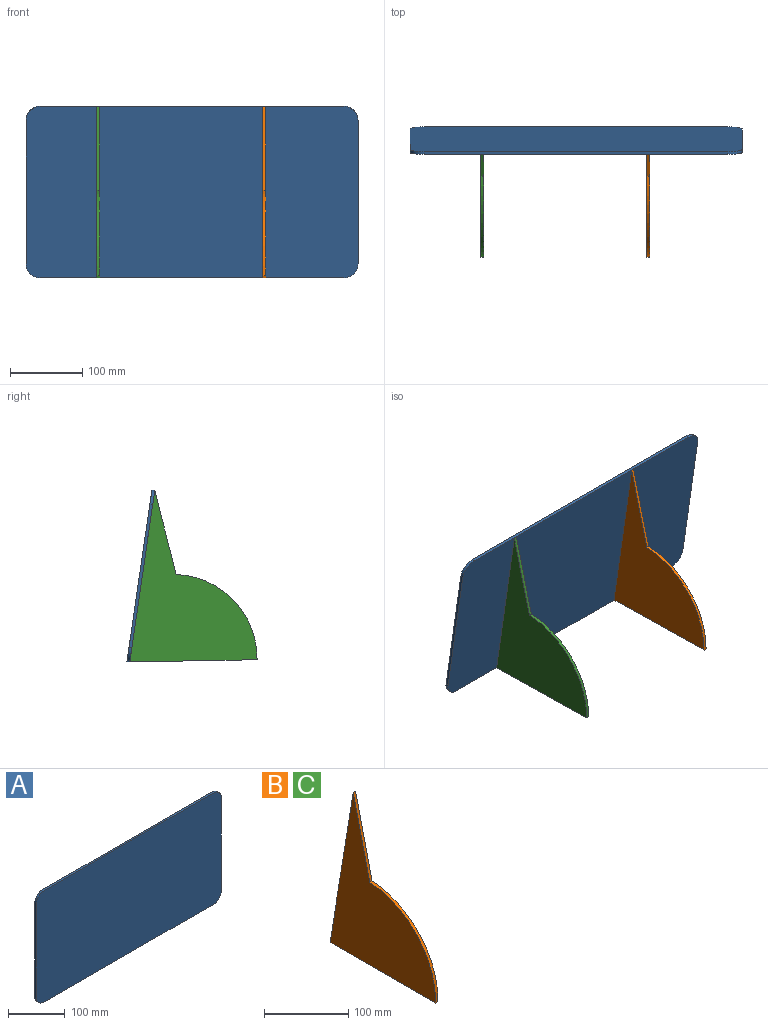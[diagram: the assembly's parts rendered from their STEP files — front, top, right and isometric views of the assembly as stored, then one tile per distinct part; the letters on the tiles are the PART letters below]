
ASSEMBLY  parts=3 mates=2
PART A: 10 faces, bbox 460x4x240 mm
  f0: plane 200x4mm, normal (1,0,0), area 800mm2, adj f1,f7,f8,f9
  f1: cylinder r=20mm len=20mm, axis (0,1,0), area 125.7mm2, adj f0,f2,f8,f9
  f2: plane 420x4mm, normal (0,0,1), area 1680mm2, adj f1,f3,f8,f9
  f3: cylinder r=20mm len=20mm, axis (0,1,0), area 125.7mm2, adj f2,f4,f8,f9
  f4: plane 200x4mm, normal (-1,0,0), area 800mm2, adj f3,f5,f8,f9
  f5: cylinder r=20mm len=20mm, axis (0,1,0), area 125.7mm2, adj f4,f6,f8,f9
  f6: plane 420x4mm, normal (0,0,-1), area 1680mm2, adj f5,f7,f8,f9
  f7: cylinder r=20mm len=20mm, axis (0,1,0), area 125.7mm2, adj f0,f6,f8,f9
  f8: plane 460x240mm, normal (0,-1,0), area 110056.6mm2, adj f0,f1,f2,f3,f4,f5,f6,f7
  f9: plane 460x240mm, normal (0,1,0), area 110056.6mm2, adj f0,f1,f2,f3,f4,f5,f6,f7
PART B: 6 faces, bbox 4x176.4x236.8 mm
  f0: plane 176.38x4mm, normal (0,0,-1), area 705.5mm2, adj f1,f3,f4,f5
  f1: plane 236.75x38.65mm, normal (0,0.99,0.16), area 959.5mm2, adj f0,f2,f4,f5
  f2: plane 116.75x27.73mm, normal (0,-0.97,0.23), area 480mm2, adj f1,f3,f4,f5
  f3: cylinder r=116.53mm len=120mm, axis (-1,0,0), area 720.9mm2, adj f0,f2,f4,f5
  f4: plane 236.75x176.44mm, normal (1,0,0), area 19834.9mm2, adj f0,f1,f2,f3
  f5: plane 236.75x176.44mm, normal (-1,0,0), area 19834.9mm2, adj f0,f1,f2,f3
PART C: same geometry as B
PLACE A rot(axis=(1,0,0),8.3deg) t=(199.3,-160.09,-44.89)mm
PLACE B rot(axis=(-1,0,0),1deg) t=(293.42,-262.79,-160.21)mm
PLACE C rot(axis=(-1,0,0),1deg) t=(63.42,-262.79,-160.21)mm
MATE fastened A.f8 <-> C.f1  axis (0,-0.99,-0.14) through (195.42,-141.39,-200.86)mm
MATE fastened A.f8 <-> B.f1  axis (0,-0.99,-0.14) through (195.42,-141.39,-200.86)mm
